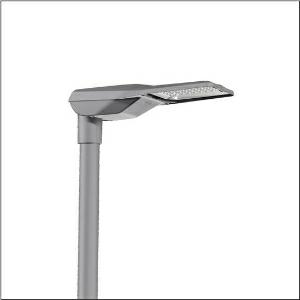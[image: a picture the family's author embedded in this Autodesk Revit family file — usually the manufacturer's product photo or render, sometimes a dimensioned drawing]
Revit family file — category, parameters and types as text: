
# Revit family: streetlight_sl_21_iq_mini___stw1_0a_5xe2e31g08jb_fb58
name_source: partatom
category: Lighting Fixtures
units: mm (PartAtom-declared; Revit-internal decimal feet)

## family parameters
Cut with Voids When Loaded = No
Host = Face
Light Source = No
Part Type = Normal
Room Calculation Point = No
Round Connector Dimension = Use Diameter
Shared = No

## types (1)
- --- (1 x LED, 10820 lm, 71.6 W, 3000K)
    Apparent Load = 72 VA
    CIE Flux Codes = 39 75 98 100 100
    Color Rendering = 70
    Color Temperature = 3000K
    Default Elevation = 1800 mm
    Description = Streetlight SL 21 mini, mast luminaire, primary light control with lens, of PMMA, primary optical cover: cover, of toughened safety glass, transparent, light distribution: STW1.0a, light emission: direct distribution, primary light characteristic: asymmetric, installation type: post-top, side-entry, LED, High Power LED, rated luminous flux: 10.820lm, luminous efficacy: 151lm/W, light colour: 730, colour temperature: 3000K, control gear: ECG iQ, control: Street-Remote, Auto-Match, Temp-Guard, Lumen-Switch, Night-Set, Smart-Wire, Light-Fading, Desk-Remote (wireless, voltage-free reading and setting of iQ features in the workshop via application-optimized NFC function/RFID function), optimised constant luminous flux control (CLO 2.0), mains connection: 220..240V, AC, 50/60Hz, start of lifetime: 72W, end of lifetime: 75W, reduction: 33W, luminaire housing, of diecast aluminium, powder-coated, Siteco® metallic grey (DB 702S), corrosivity category C5 according to DIN EN ISO 12944, length: 628mm, width: 235mm, height: 110mm, spigot size: 60/76mm (post-top) and 42/60/76mm (side-entry), mast flange for spigot size: 42mm: 5XC10008XM4, 60mm: 5XC10008XM2, 76/60mm: 5XC10108XM1, protection rating (complete): IP66, insulation class (complete): insulation class II (safety insulation), certification: CE, ENEC, VDE, impact resistance: IK09, permissible operating ambient temperature for outdoor applications: -40..+50°C, standard-compliant lighting for roads and squares, packaging unit: 1 piece

Light Distribution: STW1.0a
    Height = 110 mm
    Lamp = 1 x LED
    Lamp Light Flux = 10820 lm
    Lamp Power = 71.6 W
    Lamp count = 1
    Length = 625 mm
    Luminous efficacy = 151 lm/W
    Manufacturer = Siteco
    ModVariant = No
    Model = 5XE2E31G08JB
    Number of Poles = 1
    OnlyDefault = Yes
    Power Factor = 1
    Product Name = Streetlight SL 21 iQ mini | STW1.0a
    Product group = mast luminaire | pylon top
    ProductGroupID = 6100
    Protection Class = Protection class II
    Protection Degree = IP 66
    RLX_Detail_Level = 1
    RlxData = <blob elided: 91865 chars, md5=402d4399>
    Socket = socket
    Standby Power = 0 W
    System Light Flux = 10820 lm
    System Power = 72 W
    Type Comments = factory setting: luminous flux: 100 % | dim-lin: 254 | 746 mA
    Type Image = l_1003519.jpg
    URL = http://relux.com
    VarID = @adj_081905
    Voltage = 0 V
    Weight = 0.00 kg
    Width = 234 mm

## geometry (parser evidence)
native form markers: Blend x4, Sweep x12
no freeform markers — native parametric forms only
